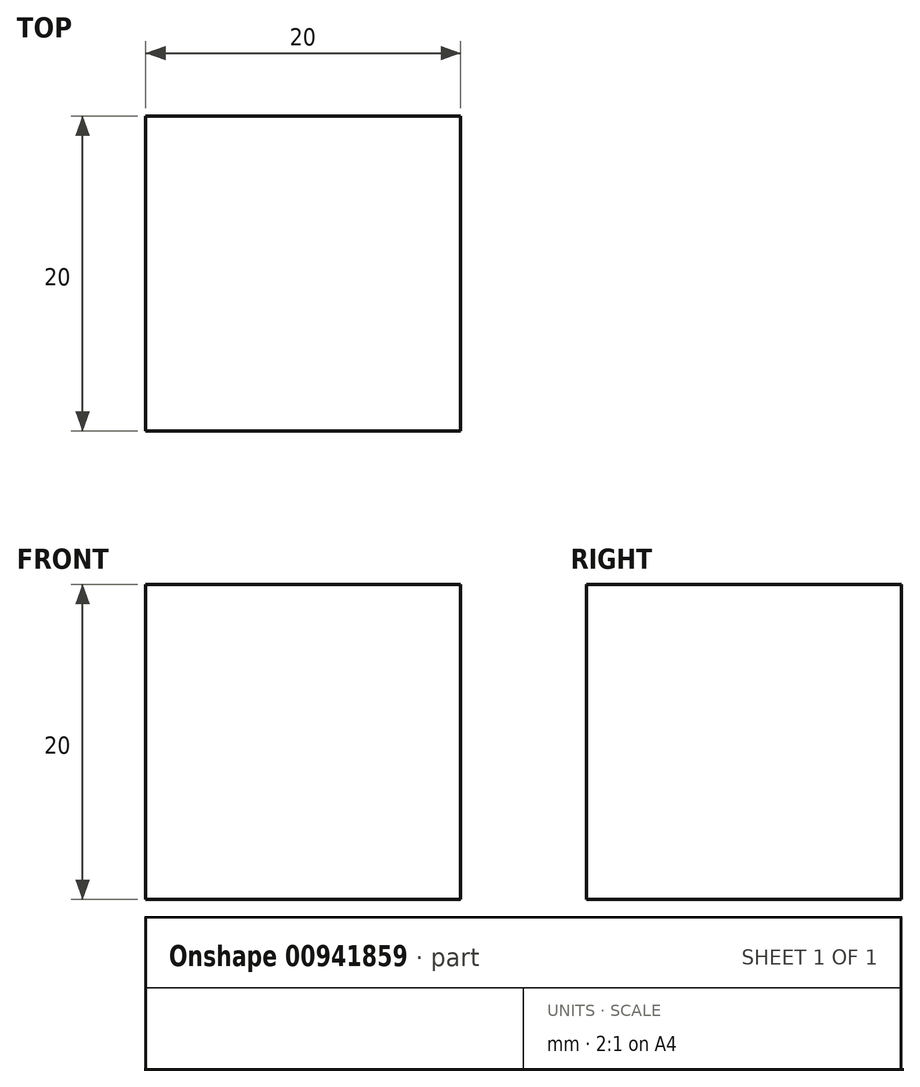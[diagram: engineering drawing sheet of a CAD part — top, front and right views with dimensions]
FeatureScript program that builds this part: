
annotation { "Feature Type Name" : "Feature", "Feature Type Description" : "" }
export const myFeature = defineFeature(function(context is Context, id is Id, definition is map)
    precondition{}
    {
        {
            var Q0;
            Q0=qCreatedBy(makeId("Top.planeOp"),FACE);
            var sketch = newSketch(context, id + "F0", { "sketchPlane" : qUnion([Q0])});
            skLineSegment(sketch, "E0.bottom", {"start": v(-21.57, 36.6) * mm, "end": v(-1.57, 36.6) * mm});
            skLineSegment(sketch, "E0.top", {"start": v(-21.57, 16.6) * mm, "end": v(-1.57, 16.6) * mm});
            skLineSegment(sketch, "E0.left", {"start": v(-21.57, 36.6) * mm, "end": v(-21.57, 16.6) * mm});
            skLineSegment(sketch, "E0.right", {"start": v(-1.57, 36.6) * mm, "end": v(-1.57, 16.6) * mm});
            skSolve(sketch);
        }
        {
            var Q0;
            Q0=makeQuery(id+"F0.imprint","IMPRINT",FACE,{"disambiguationData":[TD([[makeQuery(id+"F0.imprint","IMPRINT",EDGE,{"derivedFrom":sQuery(id+"F0.wireOp",EDGE,"E0.bottom")}),-1.0]])]});
            extrude(context, id + "F1", {"entities" : qUnion([Q0]), "depth" : 20 * mm, "offsetDistance" : 25 * mm});
        }
    });
